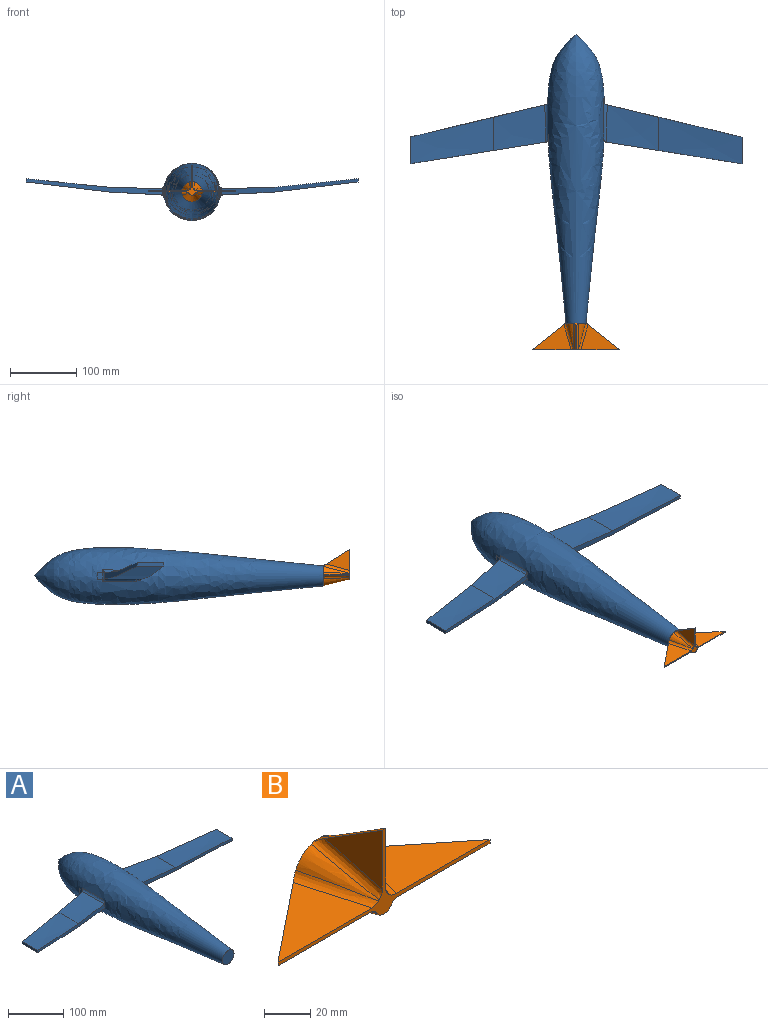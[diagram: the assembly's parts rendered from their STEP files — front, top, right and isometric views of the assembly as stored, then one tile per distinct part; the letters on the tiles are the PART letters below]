
ASSEMBLY  parts=2 mates=1
PART A: 39 faces, bbox 505.1x440.1x97.3 mm
  f0: cylinder r=42.5mm len=17.34mm, axis (0,1,0), area 94.2mm2, adj f4,f26,f28,f36
  f1: extruded ~79x68.75mm, area 4171.2mm2, adj f10,f16,f18,f26
  f2: plane 40x5.05mm, normal (1,0,0), area 201.9mm2, adj f5,f7,f21,f23
  f3: plane 40x5.05mm, normal (-1,0,0), area 201.9mm2, adj f8,f10,f16,f18
  f4: bspline ~435x92.25mm, area 85749mm2, adj f0,f11,f12,f14,f17,f19,f20,f22
  f5: extruded ~125x70mm, area 5639.6mm2, adj f2,f15,f21,f23
  f6: extruded ~79.22x68.79mm, area 4193.3mm2, adj f7,f21,f23,f29
  f7: extruded ~124.79x69.95mm, area 5655.2mm2, adj f2,f6,f21,f23
  f8: extruded ~124.79x69.95mm, area 5655.2mm2, adj f3,f9,f16,f18
  f9: extruded ~79.22x68.79mm, area 4193.3mm2, adj f8,f16,f18,f28
  f10: extruded ~125x70mm, area 5639.6mm2, adj f1,f3,f16,f18
  f11: plane 30x30mm, normal (0,-1,0), area 706.8mm2, adj f4
  f12: cylinder r=42.5mm len=17.34mm, axis (0,1,0), area 94.2mm2, adj f4,f27,f29,f35
  f13: plane 0.71x0.12mm, normal (0,1,0), area 0mm2, adj f14,f37,f38
  f14: cylinder r=42.5mm len=0.96mm, axis (0,1,0), area 0mm2, adj f4,f13,f37,f38
  f15: extruded ~79x68.75mm, area 4171.2mm2, adj f5,f21,f23,f27
  f16: plane 210.34x37.92mm, normal (0.16,-0.99,0), area 1423.7mm2, adj f1,f3,f8,f9,f10,f26,f28,f36
  f17: plane 10x0.3mm, normal (0,-1,0), area 2mm2, adj f4,f25
  f18: plane 210.28x54.32mm, normal (-0.23,0.97,0), area 1445.2mm2, adj f1,f3,f8,f9,f10,f26,f28,f30
  f19: plane 9.15x0.21mm, normal (1,0,0), area 1.9mm2, adj f4,f22,f37
  f20: extruded ~11.74x7.67mm, area 90.1mm2, adj f4,f27,f33,f34,f37,f38
  f21: plane 210.21x54.31mm, normal (0.23,0.97,0), area 1446.7mm2, adj f2,f5,f6,f7,f15,f27,f29,f33
  f22: plane 8.96x0.24mm, normal (0,-1,0), area 1.4mm2, adj f4,f19
  f23: plane 210.35x37.92mm, normal (-0.16,-0.99,0), area 1423.7mm2, adj f2,f5,f6,f7,f15,f27,f29,f35
  f24: extruded ~10x7.94mm, area 79.5mm2, adj f4,f25,f31,f32
  f25: plane 10x0mm, normal (-1,0,0), area 0mm2, adj f4,f17,f24
  f26: bspline ~69.58x6.37mm, area 375.3mm2, adj f0,f1,f4,f16,f18,f32,f36
  f27: bspline ~81.52x6.53mm, area 392mm2, adj f4,f12,f15,f20,f21,f23,f33,f35
  f28: bspline ~68.13x6.15mm, area 370.9mm2, adj f0,f4,f9,f16,f18,f30,f36
  f29: bspline ~69.53x6.24mm, area 370.9mm2, adj f4,f6,f12,f21,f23,f34,f35
  f30: bspline ~19.04x3.81mm, area 8mm2, adj f4,f18,f28,f31
  f31: cylinder r=3mm len=10.2mm, axis (0,0,1), area 39.9mm2, adj f24,f30,f32
  f32: bspline ~11.33x4.17mm, area 7.5mm2, adj f4,f18,f24,f26,f31
  f33: cylinder r=3mm len=11.89mm, axis (0,0,-1), area 42.5mm2, adj f20,f21,f27,f34
  f34: bspline ~11.31x4.03mm, area 7.2mm2, adj f4,f20,f21,f29,f33
  f35: bspline ~15.44x3.19mm, area 51.3mm2, adj f12,f23,f27,f29
  f36: bspline ~15.44x3.19mm, area 51.3mm2, adj f0,f16,f26,f28
  f37: cylinder r=0.3mm len=11.82mm, axis (0,0,-1), area 1.5mm2, adj f4,f13,f14,f19,f20,f38
  f38: bspline ~3.25x1.58mm, area 0.5mm2, adj f4,f13,f14,f20,f27,f37
PART B: 20 faces, bbox 130.3x54x55.3 mm
  f0: cone r=15mm half-angle=14deg, axis (0,1,0), area 279.7mm2, adj f3,f5,f15,f16
  f1: plane 57.65x37.44mm, normal (0,0,1), area 1071.2mm2, adj f3,f6,f16
  f2: plane 56.16x37mm, normal (0,0,-1), area 1036.1mm2, adj f3,f4,f18
  f3: plane 130.21x45.21mm, normal (0,-1,0), area 398.2mm2, adj f0,f1,f2,f4,f6,f7,f8,f9
  f4: plane 50.3x40.3mm, normal (0.62,0.78,0), area 133.8mm2, adj f2,f3,f5,f7,f17,f18
  f5: plane 30.06x30.06mm, normal (0,1,0), area 710mm2, adj f0,f4,f6,f9,f10,f11,f14,f15
  f6: plane 50.3x40.3mm, normal (-0.62,0.78,0), area 133.8mm2, adj f1,f3,f5,f8,f16,f19
  f7: plane 57.65x37.44mm, normal (0,0,1), area 1071.2mm2, adj f3,f4,f17
  f8: plane 56.16x37mm, normal (0,0,-1), area 1036.1mm2, adj f3,f6,f19
  f9: cone r=15mm half-angle=14deg, axis (0,1,0), area 989.9mm2, adj f3,f5,f18,f19
  f10: cone r=15mm half-angle=14deg, axis (0,1,0), area 279.7mm2, adj f3,f5,f14,f17
  f11: plane 40.34x25.34mm, normal (0,0.53,0.85), area 101.5mm2, adj f3,f5,f12,f13,f14,f15
  f12: plane 35.23x31.81mm, normal (1,0,0), area 556mm2, adj f3,f11,f14
  f13: plane 35.23x31.81mm, normal (-1,0,0), area 556mm2, adj f3,f11,f15
  f14: bspline ~52.53x17.9mm, area 226.6mm2, adj f3,f5,f10,f11,f12
  f15: bspline ~52.53x17.9mm, area 226.6mm2, adj f0,f3,f5,f11,f13
  f16: bspline ~52.4x18.04mm, area 217.4mm2, adj f0,f1,f3,f5,f6
  f17: bspline ~50.48x17.53mm, area 217.4mm2, adj f3,f4,f5,f7,f10
  f18: bspline ~50.18x17.21mm, area 244.9mm2, adj f2,f3,f4,f5,f9
  f19: bspline ~50.18x17.21mm, area 244.9mm2, adj f3,f5,f6,f8,f9
PLACE A t=(-226.75,92.56,-214.66)mm
PLACE B t=(-226.75,-247.44,-214.66)mm
MATE revolute A.f0 <-> B.f0  axis (0,-1,0) through (-226.75,-247.44,-214.66)mm
